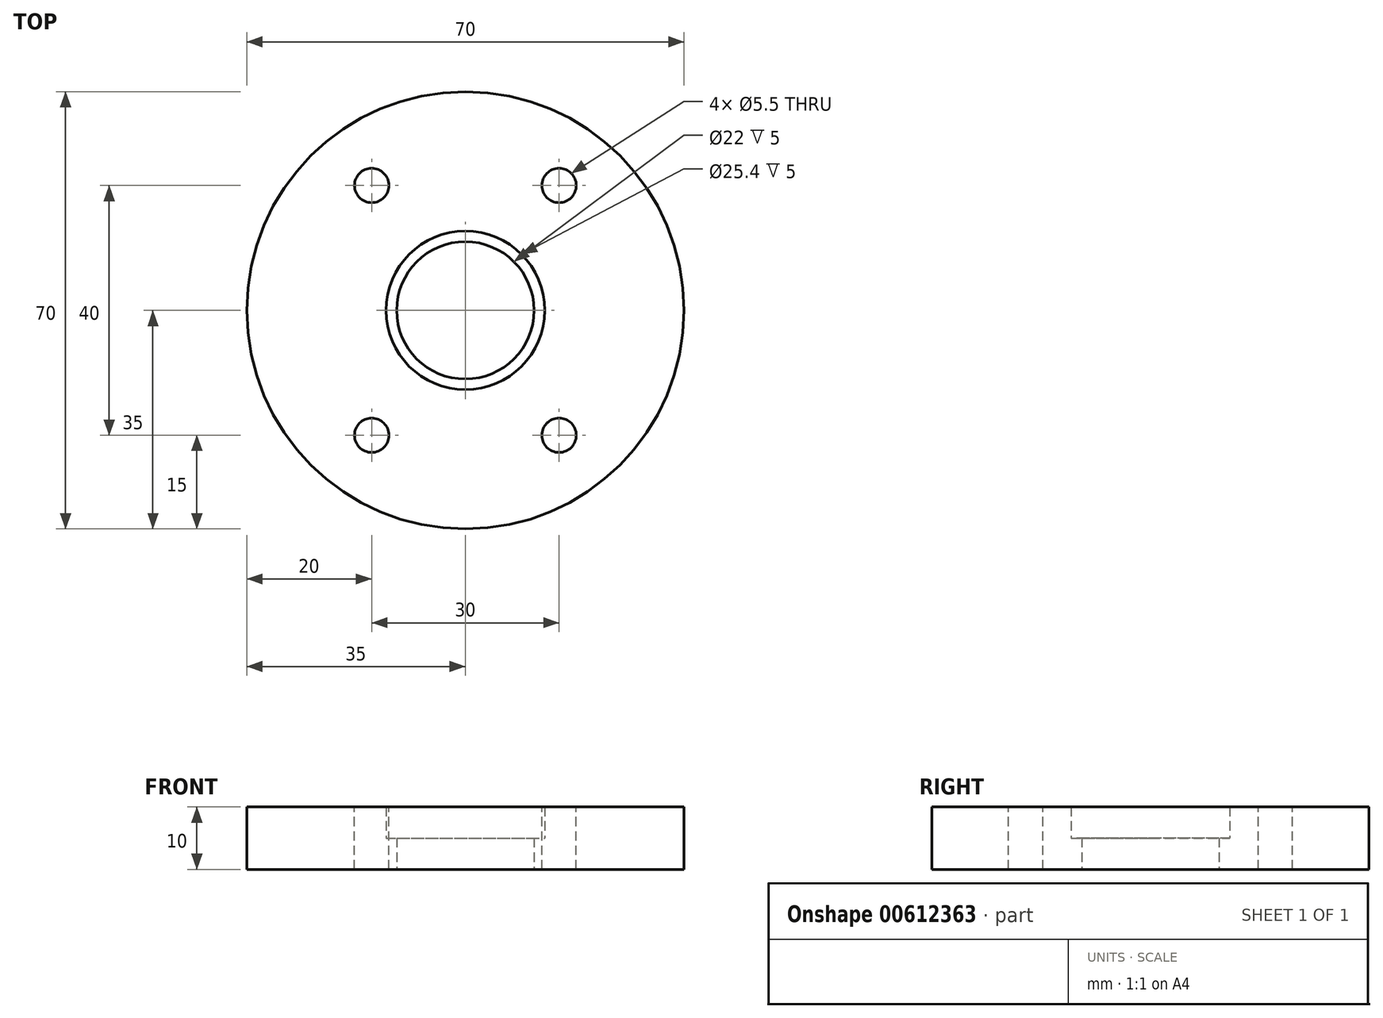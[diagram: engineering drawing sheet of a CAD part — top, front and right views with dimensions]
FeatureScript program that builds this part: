
annotation { "Feature Type Name" : "Feature", "Feature Type Description" : "" }
export const myFeature = defineFeature(function(context is Context, id is Id, definition is map)
    precondition{}
    {
        {
            var Q0;
            Q0=qCreatedBy(makeId("Front.planeOp"),FACE);
            var sketch = newSketch(context, id + "F0", { "sketchPlane" : qUnion([Q0])});
            skLineSegment(sketch, "E0", {"start": v(0, 0) * mm, "end": v(0, 12.9) * mm});
            skLineSegment(sketch, "E1", {"start": v(11, 0) * mm, "end": v(35, 0) * mm});
            skLineSegment(sketch, "E2", {"start": v(35, 0) * mm, "end": v(35, 10) * mm});
            skLineSegment(sketch, "E3", {"start": v(35, 10) * mm, "end": v(12.7, 10) * mm});
            skLineSegment(sketch, "E4", {"start": v(12.7, 10) * mm, "end": v(12.7, 5) * mm});
            skLineSegment(sketch, "E5", {"start": v(12.7, 5) * mm, "end": v(11, 5) * mm});
            skLineSegment(sketch, "E6", {"start": v(11, 5) * mm, "end": v(11, 0) * mm});
            skSolve(sketch);
        }
        {
            var Q0;
            Q0=makeQuery(id+"F0.imprint","IMPRINT",FACE,{"disambiguationData":[TD([[makeQuery(id+"F0.imprint","IMPRINT",EDGE,{"derivedFrom":sQuery(id+"F0.wireOp",EDGE,"E1")}),1.0]])]});
            var Q1;
            Q1=sQuery(id+"F0.wireOp",EDGE,"E0");
            revolve(context, id + "F1", {"entities" : qUnion([Q0]), "axis" : qUnion([Q1]), "revolveType" : RevolveType.FULL});
        }
        {
            var Q0;
            Q0=makeQuery(id+"F1.opRevolve","SWEPT_FACE",FACE,{"disambiguationData":[OSD([sQuery(id+"F0.wireOp",EDGE,"E3")])]});
            var sketch = newSketch(context, id + "F2", { "sketchPlane" : qUnion([Q0])});
            skCircle(sketch, "E7", {"center": v(-15, 20) * mm, "radius": 2.75 * mm});
            skCircle(sketch, "E8", {"center": v(15, 20) * mm, "radius": 2.75 * mm});
            skCircle(sketch, "E9", {"center": v(15, -20) * mm, "radius": 2.75 * mm});
            skCircle(sketch, "E10", {"center": v(-15, -20) * mm, "radius": 2.75 * mm});
            skSolve(sketch);
        }
        {
            var Q0;
            Q0=makeQuery(id+"F2.imprint","IMPRINT",FACE,{"disambiguationData":[TD([[makeQuery(id+"F2.imprint","IMPRINT",EDGE,{"derivedFrom":sQuery(id+"F2.wireOp",EDGE,"E7")}),1.0]])]});
            var Q1;
            Q1=makeQuery(id+"F2.imprint","IMPRINT",FACE,{"disambiguationData":[TD([[makeQuery(id+"F2.imprint","IMPRINT",EDGE,{"derivedFrom":sQuery(id+"F2.wireOp",EDGE,"E10")}),1.0]])]});
            var Q2;
            Q2=makeQuery(id+"F2.imprint","IMPRINT",FACE,{"disambiguationData":[TD([[makeQuery(id+"F2.imprint","IMPRINT",EDGE,{"derivedFrom":sQuery(id+"F2.wireOp",EDGE,"E9")}),1.0]])]});
            var Q3;
            Q3=makeQuery(id+"F2.imprint","IMPRINT",FACE,{"disambiguationData":[TD([[makeQuery(id+"F2.imprint","IMPRINT",EDGE,{"derivedFrom":sQuery(id+"F2.wireOp",EDGE,"E8")}),1.0]])]});
            extrude(context, id + "F3", {"entities" : qUnion([Q0, Q1, Q2, Q3]), "operationType" : NewBodyOperationType.REMOVE, "oppositeDirection" : true, "depth" : 10 * mm, "offsetDistance" : 25 * mm});
        }
    });
